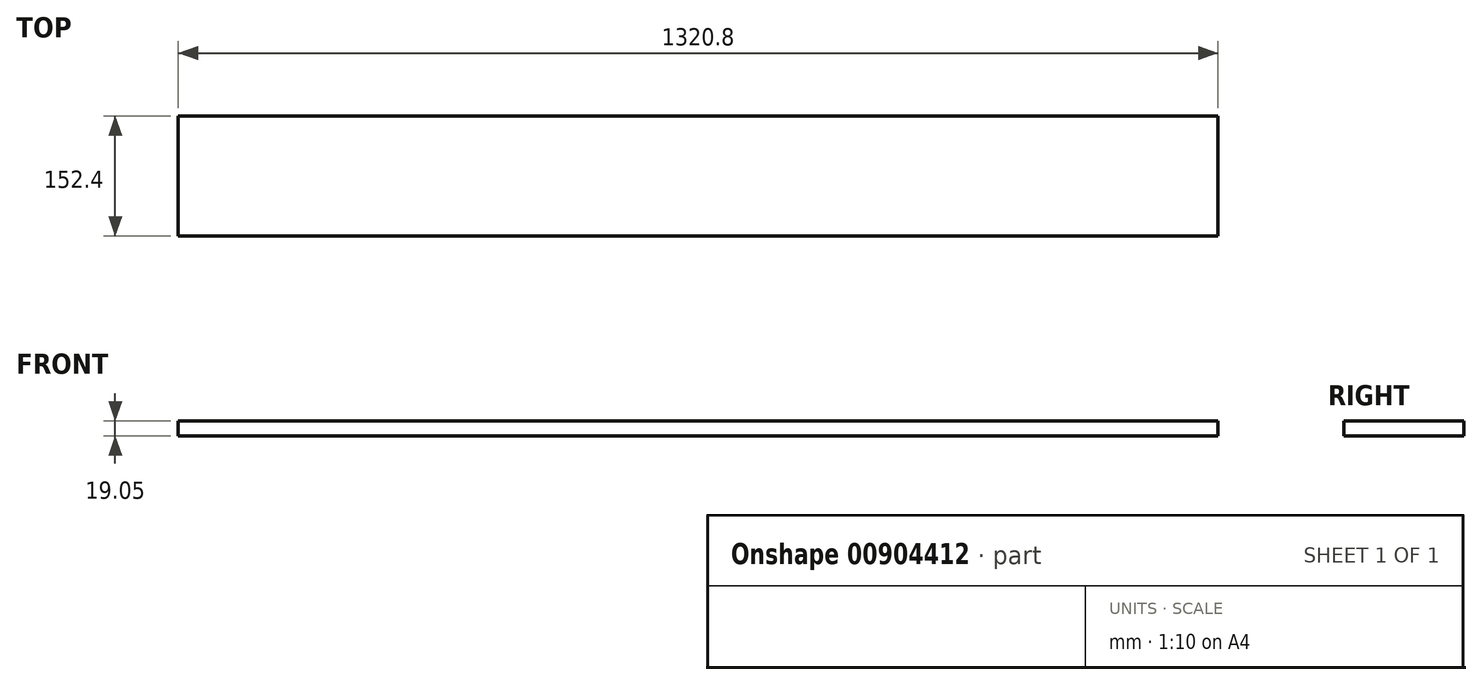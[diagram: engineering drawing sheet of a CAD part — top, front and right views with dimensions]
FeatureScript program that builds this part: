
annotation { "Feature Type Name" : "Feature", "Feature Type Description" : "" }
export const myFeature = defineFeature(function(context is Context, id is Id, definition is map)
    precondition{}
    {
        {
            var Q0;
            Q0=qCreatedBy(makeId("Top.planeOp"),FACE);
            var sketch = newSketch(context, id + "F0", { "sketchPlane" : qUnion([Q0])});
            skLineSegment(sketch, "E0.bottom", {"start": v(0, 0) * mm, "end": v(1320.8, 0) * mm});
            skLineSegment(sketch, "E0.top", {"start": v(0, 152.4) * mm, "end": v(1320.8, 152.4) * mm});
            skLineSegment(sketch, "E0.left", {"start": v(0, 0) * mm, "end": v(0, 152.4) * mm});
            skLineSegment(sketch, "E0.right", {"start": v(1320.8, 0) * mm, "end": v(1320.8, 152.4) * mm});
            skSolve(sketch);
        }
        {
            var Q0;
            Q0 = qSketchRegion(id + "F0", true);
            extrude(context, id + "F1", {"entities" : qUnion([Q0]), "depth" : 19.05 * mm, "offsetDistance" : 25.4 * mm});
        }
    });
